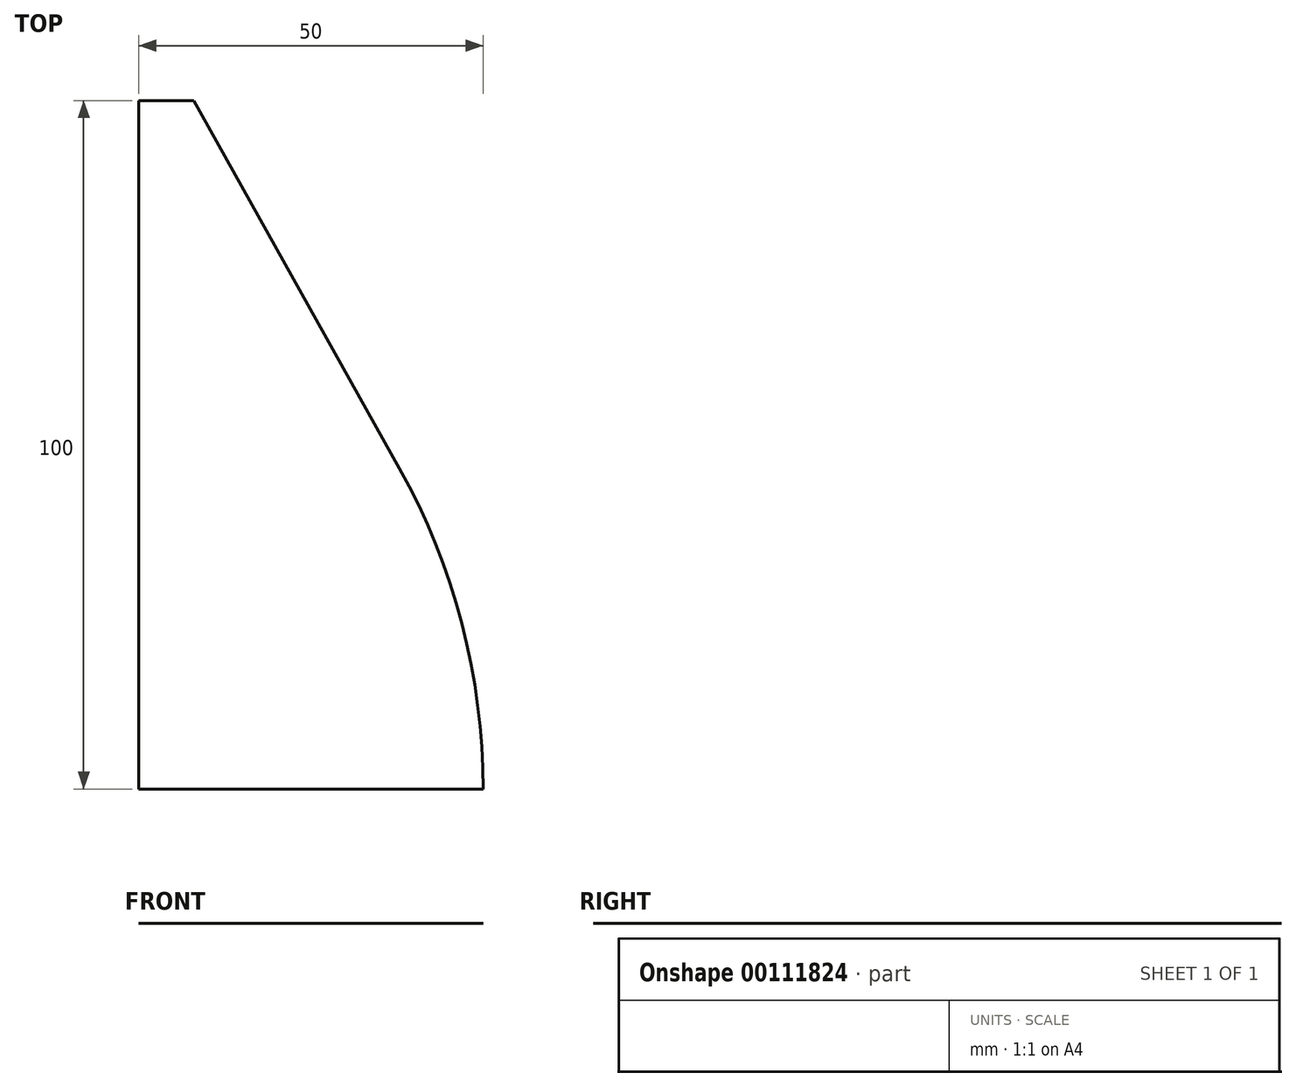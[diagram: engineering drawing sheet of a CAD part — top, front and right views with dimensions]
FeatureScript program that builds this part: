
annotation { "Feature Type Name" : "Feature", "Feature Type Description" : "" }
export const myFeature = defineFeature(function(context is Context, id is Id, definition is map)
    precondition{}
    {
        {
            var Q0;
            Q0=qCreatedBy(makeId("Top.planeOp"),FACE);
            var sketch = newSketch(context, id + "F0", { "sketchPlane" : qUnion([Q0])});
            skLineSegment(sketch, "E0.bottom", {"start": v(25, -50) * mm, "end": v(-25, -50) * mm});
            skLineSegment(sketch, "E0.top", {"start": v(-17, 50) * mm, "end": v(-25, 50) * mm});
            skLineSegment(sketch, "E0.right", {"start": v(-25, -50) * mm, "end": v(-25, 50) * mm});
            skPoint(sketch, "E0.middle", {"position": v(0, 0) * mm});
            skArc(sketch, "E1", {"start": v(25, -50) * mm, "mid": v(21.91, -25.92) * mm, "end": v(12.85, -3.4) * mm});
            skLineSegment(sketch, "E2", {"start": v(-17, 50) * mm, "end": v(12.85, -3.4) * mm});
            skPoint(sketch, "E0.left.end.orphan", {"position": v(25, 50) * mm});
            skSolve(sketch);
        }
        {
            var Q0;
            Q0 = qSketchRegion(id + "F0", true);
            extrude(context, id + "F1", {"entities" : qUnion([Q0]), "depth" : 1 / 203.2 * mm});
        }
    });
